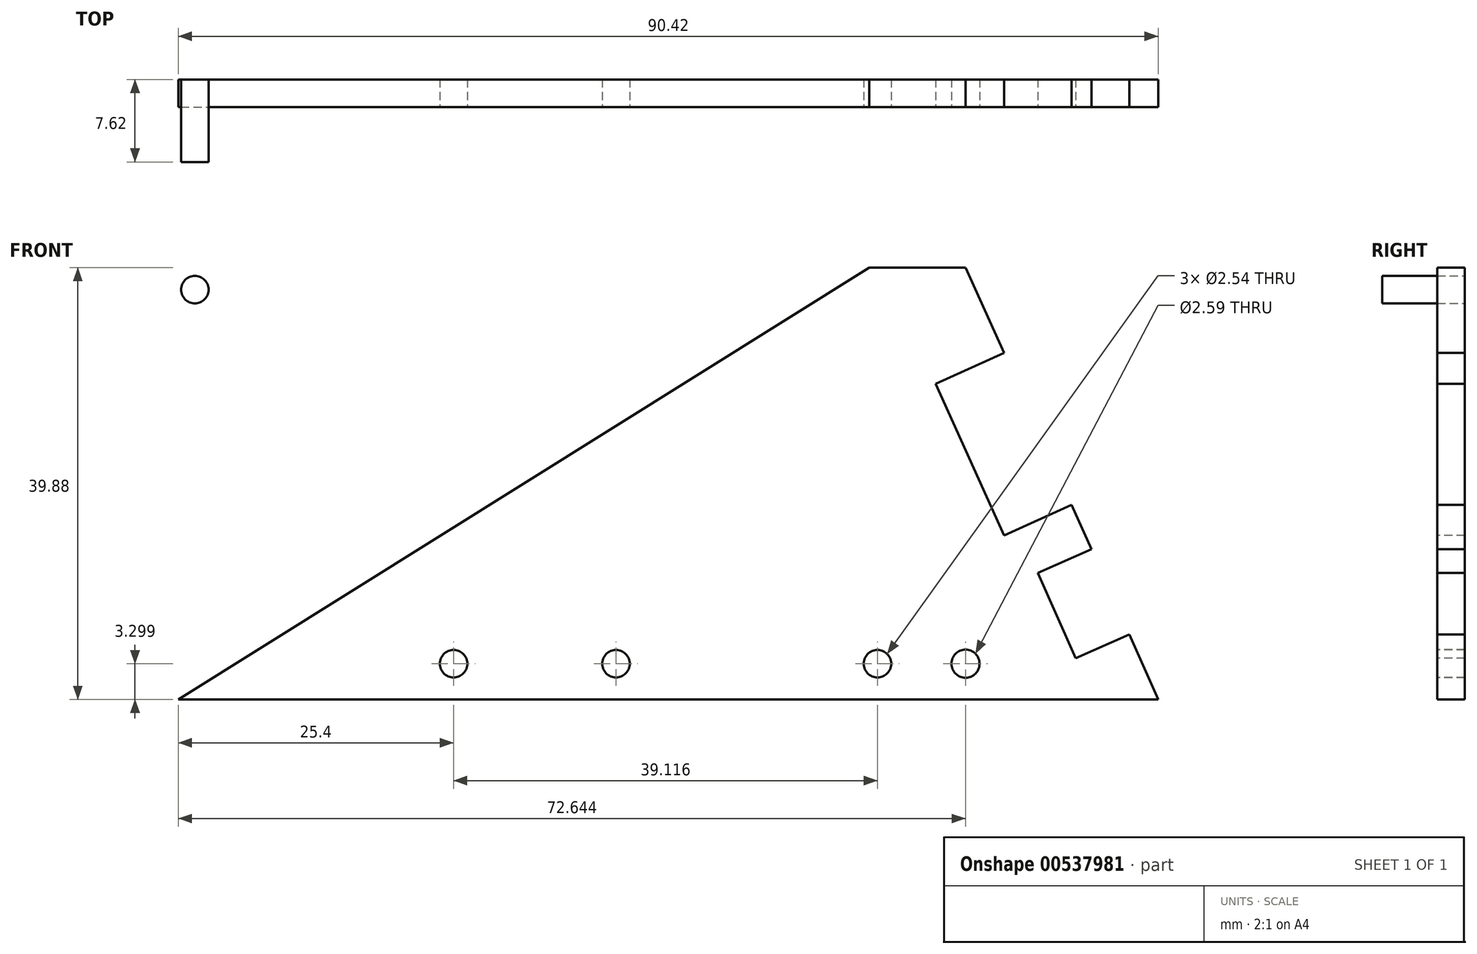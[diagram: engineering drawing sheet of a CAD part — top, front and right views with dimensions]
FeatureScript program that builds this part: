
annotation { "Feature Type Name" : "Feature", "Feature Type Description" : "" }
export const myFeature = defineFeature(function(context is Context, id is Id, definition is map)
    precondition{}
    {
        {
            var Q0;
            Q0=qCreatedBy(makeId("Front.planeOp"),FACE);
            var sketch = newSketch(context, id + "F0", { "sketchPlane" : qUnion([Q0])});
            skLineSegment(sketch, "E0", {"start": v(-55.88, 0) * mm, "end": v(7.87, 39.88) * mm});
            skLineSegment(sketch, "E1", {"start": v(7.87, 39.88) * mm, "end": v(16.76, 39.88) * mm});
            skLineSegment(sketch, "E2", {"start": v(16.76, 39.88) * mm, "end": v(20.32, 32) * mm});
            skLineSegment(sketch, "E3", {"start": v(20.32, 32) * mm, "end": v(34.54, 0) * mm});
            skLineSegment(sketch, "E4", {"start": v(34.54, 0) * mm, "end": v(-55.88, 0) * mm});
            skSolve(sketch);
        }
        {
            var Q0;
            Q0 = qSketchRegion(id + "F0", true);
            extrude(context, id + "F1", {"entities" : qUnion([Q0]), "depth" : 2.54 * mm, "offsetDistance" : 25.4 * mm});
        }
        {
            var Q0;
            Q0=makeQuery(id+"F1.opExtrude","CAP_FACE",FACE,{"disambiguationData":[OSD([sQuery(id+"F0.wireOp",EDGE,"E0"),sQuery(id+"F0.wireOp",EDGE,"E1"),sQuery(id+"F0.wireOp",EDGE,"E2"),sQuery(id+"F0.wireOp",EDGE,"E3"),sQuery(id+"F0.wireOp",EDGE,"E4")])],"isStart":false});
            var sketch = newSketch(context, id + "F2", { "sketchPlane" : qUnion([Q0])});
            skLineSegment(sketch, "E5", {"start": v(20.32, 32) * mm, "end": v(14, 29.15) * mm});
            skLineSegment(sketch, "E6", {"start": v(14, 29.15) * mm, "end": v(20.32, 15.15) * mm});
            skLineSegment(sketch, "E7", {"start": v(20.32, 15.15) * mm, "end": v(26.56, 17.96) * mm});
            skSolve(sketch);
        }
        {
            var Q0;
            Q0 = qSketchRegion(id + "F2", true);
            var Q1;
            {var subQ0=sQuery(id+"F2.wireOp",EDGE,"E5");Q1=makeQuery(id+"F2.imprint","IMPRINT",FACE,{"disambiguationData":[TD([[makeQuery(id+"F2.imprint","IMPRINT",EDGE,{"derivedFrom":subQ0}),1.0]])]});}
            extrude(context, id + "F3", {"entities" : qUnion([Q0, Q1]), "operationType" : NewBodyOperationType.REMOVE, "oppositeDirection" : true, "depth" : 25.4 * mm, "offsetDistance" : 25.4 * mm});
        }
        {
            var Q0;
            Q0=makeQuery(id+"F1.opExtrude","CAP_FACE",FACE,{"disambiguationData":[OSD([sQuery(id+"F0.wireOp",EDGE,"E0"),sQuery(id+"F0.wireOp",EDGE,"E1"),sQuery(id+"F0.wireOp",EDGE,"E2"),sQuery(id+"F0.wireOp",EDGE,"E3"),sQuery(id+"F0.wireOp",EDGE,"E4")])],"isStart":false});
            var sketch = newSketch(context, id + "F4", { "sketchPlane" : qUnion([Q0])});
            skLineSegment(sketch, "E8", {"start": v(23.44, 11.68) * mm, "end": v(26.92, 3.8) * mm});
            skPoint(sketch, "E8.startSnap0", {"position": v(23.44, 16.56) * mm});
            skLineSegment(sketch, "E9", {"start": v(26.92, 3.8) * mm, "end": v(31.88, 6) * mm});
            skLineSegment(sketch, "E10", {"start": v(23.44, 11.68) * mm, "end": v(28.38, 13.88) * mm});
            skLineSegment(sketch, "E11", {"start": v(28.38, 13.88) * mm, "end": v(31.88, 6) * mm});
            skSolve(sketch);
        }
        {
            var Q0;
            Q0 = qSketchRegion(id + "F4", true);
            extrude(context, id + "F5", {"entities" : qUnion([Q0]), "operationType" : NewBodyOperationType.REMOVE, "oppositeDirection" : true, "depth" : 25.4 * mm, "offsetDistance" : 25.4 * mm});
        }
        {
            var Q0;
            Q0=makeQuery(id+"F1.opExtrude","SWEPT_FACE",FACE,{"disambiguationData":[OSD([sQuery(id+"F0.wireOp",EDGE,"E4")])]});
            var sketch = newSketch(context, id + "F6", { "sketchPlane" : qUnion([Q0])});
            skCircle(sketch, "E12", {"center": v(-50.8, 1.27) * mm, "radius": 1.63 * mm});
            skPoint(sketch, "E12.centerSnap0", {"position": v(-55.88, 1.27) * mm});
            skCircle(sketch, "E13", {"center": v(-36.83, 1.27) * mm, "radius": 1.6 * mm});
            skCircle(sketch, "E14", {"center": v(-21.84, 1.27) * mm, "radius": 1.78 * mm});
            skCircle(sketch, "E15", {"center": v(-5.33, 1.27) * mm, "radius": 1.8 * mm});
            skCircle(sketch, "E16", {"center": v(9.14, 1.27) * mm, "radius": 1.93 * mm});
            skCircle(sketch, "E17", {"center": v(23.11, 1.27) * mm, "radius": 1.8 * mm});
            skSolve(sketch);
        }
        {
            var Q0;
            Q0 = qSketchRegion(id + "F6", true);
            extrude(context, id + "F7", {"entities" : qUnion([Q0]), "endBound" : BoundingType.SYMMETRIC, "depth" : 10.16 * mm, "offsetDistance" : 25.4 * mm});
        }
        {
            var Q0;
            Q0=makeQuery(id+"F7.opExtrude","SWEPT_BODY",BODY,{"disambiguationData":[OSD([sQuery(id+"F6.wireOp",EDGE,"E12")])]});
            deleteBodies(context, id + "F8", {"entities" : qUnion([Q0])});
        }
        {
            var Q0;
            Q0=makeQuery(id+"F7.opExtrude","SWEPT_BODY",BODY,{"disambiguationData":[OSD([sQuery(id+"F6.wireOp",EDGE,"E13")])]});
            var Q1;
            Q1=makeQuery(id+"F7.opExtrude","SWEPT_BODY",BODY,{"disambiguationData":[OSD([sQuery(id+"F6.wireOp",EDGE,"E14")])]});
            var Q2;
            Q2=makeQuery(id+"F7.opExtrude","SWEPT_BODY",BODY,{"disambiguationData":[OSD([sQuery(id+"F6.wireOp",EDGE,"E15")])]});
            var Q3;
            Q3=makeQuery(id+"F7.opExtrude","SWEPT_BODY",BODY,{"disambiguationData":[OSD([sQuery(id+"F6.wireOp",EDGE,"E16")])]});
            var Q4;
            Q4=makeQuery(id+"F7.opExtrude","SWEPT_BODY",BODY,{"disambiguationData":[OSD([sQuery(id+"F6.wireOp",EDGE,"E17")])]});
            deleteBodies(context, id + "F9", {"entities" : qUnion([Q0, Q1, Q2, Q3, Q4])});
        }
        {
            var Q0;
            Q0=makeQuery(id+"F1.opExtrude","SWEPT_FACE",FACE,{"disambiguationData":[OSD([sQuery(id+"F0.wireOp",EDGE,"E4")])]});
            var sketch = newSketch(context, id + "F10", { "sketchPlane" : qUnion([Q0])});
            skCircle(sketch, "E18", {"center": v(-31.75, 4.06) * mm, "radius": 1.3 * mm});
            skCircle(sketch, "E19", {"center": v(-17.53, 4.32) * mm, "radius": 1.3 * mm});
            skCircle(sketch, "E20", {"center": v(-4.83, 4.32) * mm, "radius": 1.3 * mm});
            skCircle(sketch, "E21", {"center": v(8.9, 4.06) * mm, "radius": 1.3 * mm});
            skSolve(sketch);
        }
        {
            var Q0;
            Q0=makeQuery(id+"F10.imprint","IMPRINT",FACE,{"disambiguationData":[TD([[makeQuery(id+"F10.imprint","IMPRINT",EDGE,{"derivedFrom":sQuery(id+"F10.wireOp",EDGE,"E18")}),1.0]])]});
            var Q1;
            Q1=makeQuery(id+"F10.imprint","IMPRINT",FACE,{"disambiguationData":[TD([[makeQuery(id+"F10.imprint","IMPRINT",EDGE,{"derivedFrom":sQuery(id+"F10.wireOp",EDGE,"E19")}),1.0]])]});
            var Q2;
            Q2=makeQuery(id+"F10.imprint","IMPRINT",FACE,{"disambiguationData":[TD([[makeQuery(id+"F10.imprint","IMPRINT",EDGE,{"derivedFrom":sQuery(id+"F10.wireOp",EDGE,"E20")}),1.0]])]});
            var Q3;
            Q3=makeQuery(id+"F10.imprint","IMPRINT",FACE,{"disambiguationData":[TD([[makeQuery(id+"F10.imprint","IMPRINT",EDGE,{"derivedFrom":sQuery(id+"F10.wireOp",EDGE,"E21")}),1.0]])]});
            extrude(context, id + "F11", {"entities" : qUnion([Q0, Q1, Q2, Q3]), "operationType" : NewBodyOperationType.REMOVE, "oppositeDirection" : true, "depth" : 12.7 * mm, "offsetDistance" : 25.4 * mm});
        }
        {
            var Q0;
            Q0=makeQuery(id+"F1.opExtrude","CAP_FACE",FACE,{"disambiguationData":[OSD([sQuery(id+"F0.wireOp",EDGE,"E0"),sQuery(id+"F0.wireOp",EDGE,"E1"),sQuery(id+"F0.wireOp",EDGE,"E2"),sQuery(id+"F0.wireOp",EDGE,"E3"),sQuery(id+"F0.wireOp",EDGE,"E4")])],"isStart":false});
            var sketch = newSketch(context, id + "F12", { "sketchPlane" : qUnion([Q0])});
            skCircle(sketch, "E22", {"center": v(-30.48, 3.3) * mm, "radius": 1.27 * mm});
            skCircle(sketch, "E23", {"center": v(-15.5, 3.3) * mm, "radius": 1.27 * mm});
            skCircle(sketch, "E24", {"center": v(8.64, 3.3) * mm, "radius": 1.27 * mm});
            skCircle(sketch, "E25", {"center": v(16.76, 3.3) * mm, "radius": 1.3 * mm});
            skSolve(sketch);
        }
        {
            var Q0;
            Q0=makeQuery(id+"F12.imprint","IMPRINT",FACE,{"disambiguationData":[TD([[makeQuery(id+"F12.imprint","IMPRINT",EDGE,{"derivedFrom":sQuery(id+"F12.wireOp",EDGE,"E22")}),1.0]])]});
            var Q1;
            Q1=makeQuery(id+"F12.imprint","IMPRINT",FACE,{"disambiguationData":[TD([[makeQuery(id+"F12.imprint","IMPRINT",EDGE,{"derivedFrom":sQuery(id+"F12.wireOp",EDGE,"E23")}),1.0]])]});
            var Q2;
            Q2=makeQuery(id+"F12.imprint","IMPRINT",FACE,{"disambiguationData":[TD([[makeQuery(id+"F12.imprint","IMPRINT",EDGE,{"derivedFrom":sQuery(id+"F12.wireOp",EDGE,"E24")}),1.0]])]});
            var Q3;
            Q3=makeQuery(id+"F12.imprint","IMPRINT",FACE,{"disambiguationData":[TD([[makeQuery(id+"F12.imprint","IMPRINT",EDGE,{"derivedFrom":sQuery(id+"F12.wireOp",EDGE,"E25")}),1.0]])]});
            extrude(context, id + "F13", {"entities" : qUnion([Q0, Q1, Q2, Q3]), "operationType" : NewBodyOperationType.REMOVE, "oppositeDirection" : true, "depth" : 2.54 * mm, "offsetDistance" : 25.4 * mm});
        }
        {
            var Q0;
            Q0=qCreatedBy(makeId("Front.planeOp"),FACE);
            var sketch = newSketch(context, id + "F14", { "sketchPlane" : qUnion([Q0])});
            skCircle(sketch, "E26", {"center": v(-54.36, 37.84) * mm, "radius": 1.27 * mm});
            skSolve(sketch);
        }
        {
            var Q0;
            Q0 = qSketchRegion(id + "F14", true);
            extrude(context, id + "F15", {"entities" : qUnion([Q0]), "depth" : 7.62 * mm, "offsetDistance" : 25.4 * mm});
        }
    });
